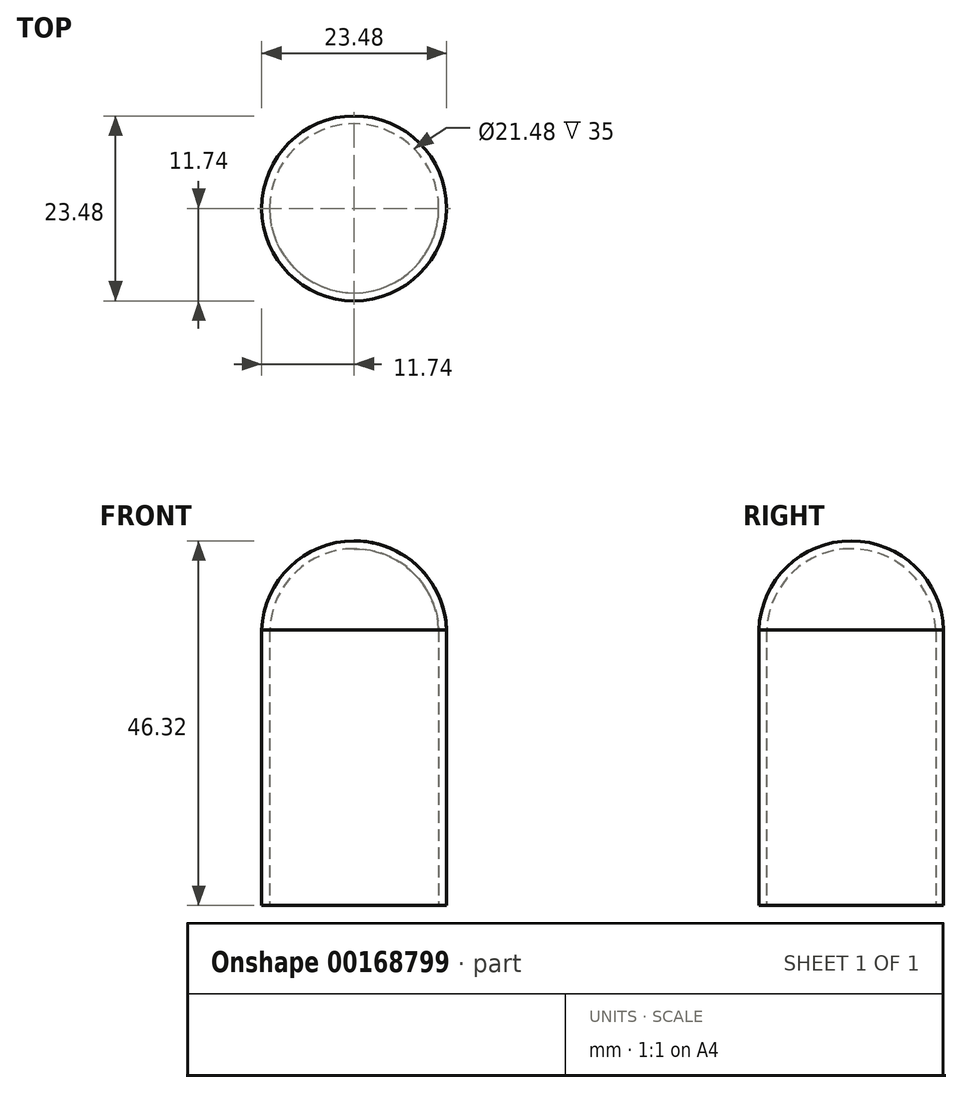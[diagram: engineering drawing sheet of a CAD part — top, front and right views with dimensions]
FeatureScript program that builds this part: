
annotation { "Feature Type Name" : "Feature", "Feature Type Description" : "" }
export const myFeature = defineFeature(function(context is Context, id is Id, definition is map)
    precondition{}
    {
        {
            var Q0;
            Q0=qCreatedBy(makeId("Front.planeOp"),FACE);
            var sketch = newSketch(context, id + "F0", { "sketchPlane" : qUnion([Q0])});
            skArc(sketch, "E0", {"start": v(0, 46.32) * mm, "mid": v(-8.16, 43.03) * mm, "end": v(-11.74, 35) * mm});
            skArc(sketch, "E1", {"start": v(0, 45.32) * mm, "mid": v(-7.45, 42.32) * mm, "end": v(-10.74, 35) * mm});
            skLineSegment(sketch, "E2", {"start": v(-11.74, 35) * mm, "end": v(-11.74, 0) * mm});
            skLineSegment(sketch, "E3", {"start": v(-10.74, 35) * mm, "end": v(-10.74, 0) * mm});
            skLineSegment(sketch, "E4", {"start": v(-11.74, 0) * mm, "end": v(-10.74, 0) * mm});
            skLineSegment(sketch, "E5", {"start": v(0, 45.32) * mm, "end": v(0, 46.32) * mm});
            skLineSegment(sketch, "E6", {"start": v(-11.74, 35) * mm, "end": v(-10.74, 35) * mm, "construction": true});
            skLineSegment(sketch, "E7", {"start": v(0, -15.7) * mm, "end": v(0, 17.31) * mm, "construction": true});
            skSolve(sketch);
        }
        {
            var Q0;
            Q0 = qSketchRegion(id + "F0", true);
            var Q1;
            Q1=sQuery(id+"F0.wireOp",EDGE,"E7");
            revolve(context, id + "F1", {"entities" : qUnion([Q0]), "axis" : qUnion([Q1]), "revolveType" : RevolveType.FULL});
        }
    });
